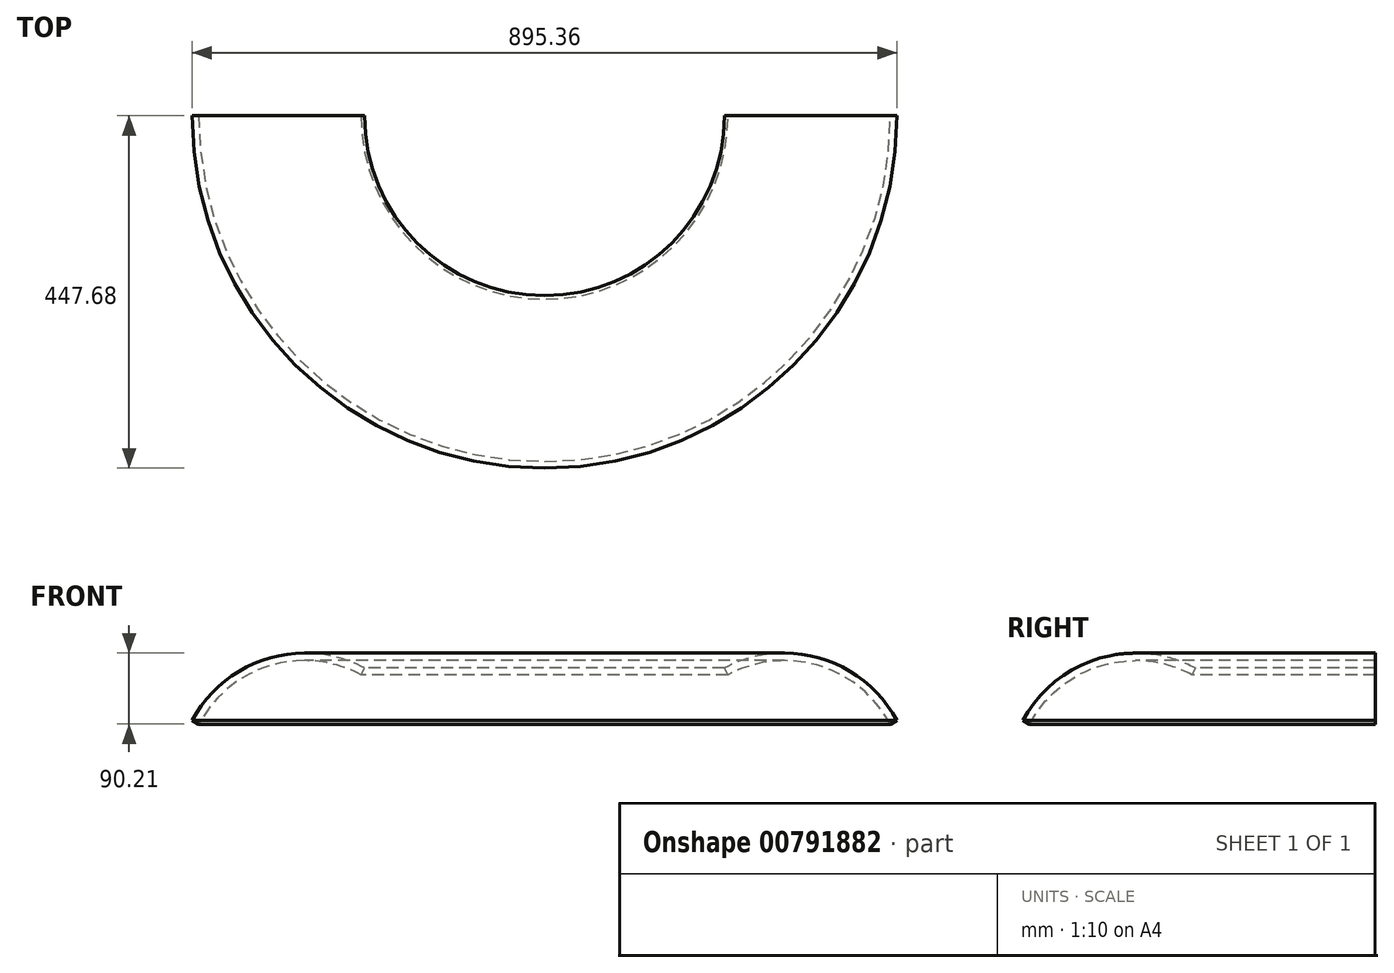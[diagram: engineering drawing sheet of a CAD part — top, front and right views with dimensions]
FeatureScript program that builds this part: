
annotation { "Feature Type Name" : "Feature", "Feature Type Description" : "" }
export const myFeature = defineFeature(function(context is Context, id is Id, definition is map)
    precondition{}
    {
        {
            var Q0;
            Q0=qCreatedBy(makeId("Front.planeOp"),FACE);
            var sketch = newSketch(context, id + "F0", { "sketchPlane" : qUnion([Q0])});
            skArc(sketch, "E0", {"start": v(-233.08, 134.47) * mm, "mid": v(-349.17, 145.8) * mm, "end": v(-439.27, 71.72) * mm});
            skArc(sketch, "E1", {"start": v(-228.6, 142.88) * mm, "mid": v(-351.95, 154.9) * mm, "end": v(-447.68, 76.2) * mm});
            skLineSegment(sketch, "E2", {"start": v(0, 0) * mm, "end": v(0, 304.8) * mm});
            skLineSegment(sketch, "E3", {"start": v(-233.08, 134.47) * mm, "end": v(-228.6, 142.88) * mm});
            skLineSegment(sketch, "E4", {"start": v(-439.27, 71.72) * mm, "end": v(-447.68, 76.2) * mm});
            skSolve(sketch);
        }
        {
            var Q0;
            Q0=makeQuery(id+"F0.imprint","IMPRINT",FACE,{"disambiguationData":[TD([[makeQuery(id+"F0.imprint","IMPRINT",EDGE,{"derivedFrom":sQuery(id+"F0.wireOp",EDGE,"E0")}),-1.0]])]});
            var Q1;
            Q1=sQuery(id+"F0.wireOp",EDGE,"E0");
            var Q2;
            Q2=sQuery(id+"F0.wireOp",EDGE,"E1");
            var Q3;
            Q3=sQuery(id+"F0.wireOp",EDGE,"E2");
            revolve(context, id + "F1", {"surfaceOperationType" : NewSurfaceOperationType.NEW, "entities" : qUnion([Q0]), "surfaceEntities" : qUnion([Q1, Q2]), "axis" : qUnion([Q3]), "revolveType" : RevolveType.ONE_DIRECTION, "angle" : 180 * degree});
        }
    });
